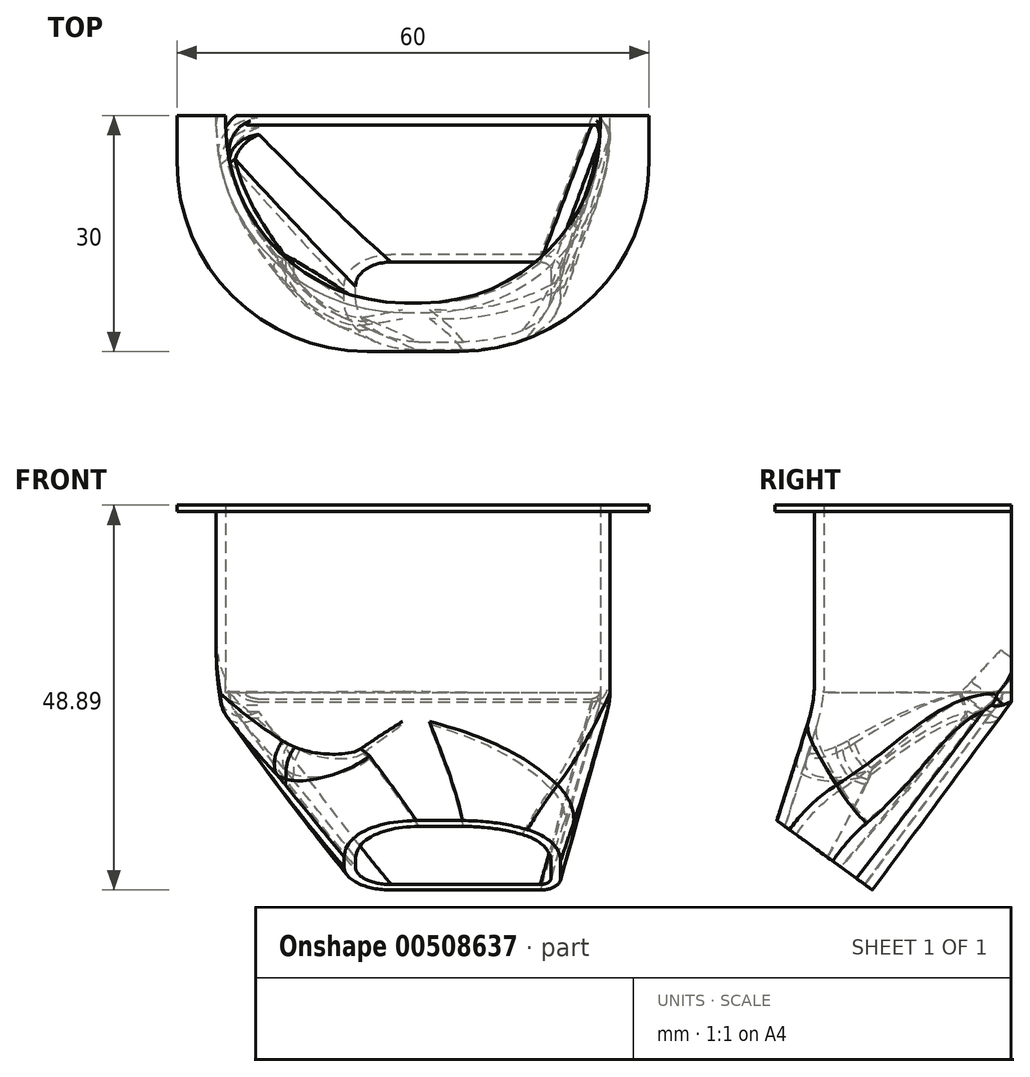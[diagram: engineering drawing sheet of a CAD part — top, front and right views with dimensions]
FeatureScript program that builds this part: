
annotation { "Feature Type Name" : "Feature", "Feature Type Description" : "" }
export const myFeature = defineFeature(function(context is Context, id is Id, definition is map)
    precondition{}
    {
        {
            var Q0;
            Q0=qCreatedBy(makeId("Front.planeOp"),FACE);
            var sketch = newSketch(context, id + "F0", { "sketchPlane" : qUnion([Q0])});
            skLineSegment(sketch, "E0.bottom", {"start": v(-25, 25) * mm, "end": v(25, 25) * mm});
            skLineSegment(sketch, "E0.top", {"start": v(-25, 0) * mm, "end": v(25, 0) * mm});
            skLineSegment(sketch, "E0.left", {"start": v(-25, 25) * mm, "end": v(-25, 0) * mm});
            skLineSegment(sketch, "E0.right", {"start": v(25, 25) * mm, "end": v(25, 0) * mm});
            skSolve(sketch);
        }
        {
            var Q0;
            Q0=makeQuery(id+"F0.imprint","IMPRINT",FACE,{"disambiguationData":[TD([[makeQuery(id+"F0.imprint","IMPRINT",EDGE,{"derivedFrom":sQuery(id+"F0.wireOp",EDGE,"E0.bottom")}),-1.0]])]});
            extrude(context, id + "F1", {"entities" : qUnion([Q0]), "endBound" : BoundingType.SYMMETRIC, "depth" : 25 * mm});
        }
        {
            var Q0;
            Q0=makeQuery(id+"F1.opExtrude","SWEPT_FACE",FACE,{"disambiguationData":[OSD([sQuery(id+"F0.wireOp",EDGE,"E0.bottom")])]});
            var Q1;
            Q1=makeQuery(id+"F1.opExtrude","CAP_FACE",FACE,{"disambiguationData":[OSD([sQuery(id+"F0.wireOp",EDGE,"E0.bottom"),sQuery(id+"F0.wireOp",EDGE,"E0.top"),sQuery(id+"F0.wireOp",EDGE,"E0.left"),sQuery(id+"F0.wireOp",EDGE,"E0.right")])],"isStart":true});
            shell(context, id + "F2", {"entities" : qUnion([Q0, Q1]), "thickness" : 1.2 * mm});
        }
        {
            var Q0;
            Q0=makeQuery(id+"F1.opExtrude","SWEPT_FACE",FACE,{"disambiguationData":[OSD([sQuery(id+"F0.wireOp",EDGE,"E0.right")])]});
            var sketch = newSketch(context, id + "F3", { "sketchPlane" : qUnion([Q0])});
            skLineSegment(sketch, "E1.bottom", {"start": v(-12.5, 25) * mm, "end": v(12.5, 25) * mm});
            skLineSegment(sketch, "E1.top", {"start": v(-12.5, 24.2) * mm, "end": v(12.5, 24.2) * mm});
            skLineSegment(sketch, "E1.left", {"start": v(-12.5, 25) * mm, "end": v(-12.5, 24.2) * mm});
            skLineSegment(sketch, "E1.right", {"start": v(12.5, 25) * mm, "end": v(12.5, 24.2) * mm});
            skSolve(sketch);
        }
        {
            var Q0;
            Q0=makeQuery(id+"F3.imprint","IMPRINT",FACE,{"disambiguationData":[TD([[makeQuery(id+"F3.imprint","IMPRINT",EDGE,{"derivedFrom":sQuery(id+"F3.wireOp",EDGE,"E1.bottom")}),-1.0]])]});
            extrude(context, id + "F4", {"entities" : qUnion([Q0]), "operationType" : NewBodyOperationType.ADD, "depth" : 5 * mm});
        }
        {
            var Q0;
            Q0=makeQuery(id+"F1.opExtrude","SWEPT_FACE",FACE,{"disambiguationData":[OSD([sQuery(id+"F0.wireOp",EDGE,"E0.left")])]});
            var sketch = newSketch(context, id + "F5", { "sketchPlane" : qUnion([Q0])});
            skLineSegment(sketch, "E2.bottom", {"start": v(-12.5, 25) * mm, "end": v(12.5, 25) * mm});
            skLineSegment(sketch, "E2.top", {"start": v(-12.5, 24.2) * mm, "end": v(12.5, 24.2) * mm});
            skLineSegment(sketch, "E2.left", {"start": v(-12.5, 25) * mm, "end": v(-12.5, 24.2) * mm});
            skLineSegment(sketch, "E2.right", {"start": v(12.5, 25) * mm, "end": v(12.5, 24.2) * mm});
            skSolve(sketch);
        }
        {
            var Q0;
            Q0=makeQuery(id+"F5.imprint","IMPRINT",FACE,{"disambiguationData":[TD([[makeQuery(id+"F5.imprint","IMPRINT",EDGE,{"derivedFrom":sQuery(id+"F5.wireOp",EDGE,"E2.bottom")}),1.0]])]});
            extrude(context, id + "F6", {"entities" : qUnion([Q0]), "operationType" : NewBodyOperationType.ADD, "depth" : 5 * mm});
        }
        {
            var Q0;
            Q0=makeQuery(id+"F6.boolean.opBoolean","MERGE",FACE,{"derivedFrom":[makeQuery(id+"F4.boolean.opBoolean","MERGE",FACE,{"derivedFrom":[makeQuery(id+"F1.opExtrude","CAP_FACE",FACE,{"disambiguationData":[OSD([sQuery(id+"F0.wireOp",EDGE,"E0.bottom"),sQuery(id+"F0.wireOp",EDGE,"E0.top"),sQuery(id+"F0.wireOp",EDGE,"E0.left"),sQuery(id+"F0.wireOp",EDGE,"E0.right")])],"isStart":false}),makeQuery(id+"F4.opExtrude","SWEPT_FACE",FACE,{"disambiguationData":[OSD([sQuery(id+"F3.wireOp",EDGE,"E1.left")])]})]}),makeQuery(id+"F6.opExtrude","SWEPT_FACE",FACE,{"disambiguationData":[OSD([sQuery(id+"F5.wireOp",EDGE,"E2.right")])]})]});
            var sketch = newSketch(context, id + "F7", { "sketchPlane" : qUnion([Q0])});
            skLineSegment(sketch, "E3.bottom", {"start": v(-30, 25) * mm, "end": v(30, 25) * mm});
            skLineSegment(sketch, "E3.top", {"start": v(-30, 24.2) * mm, "end": v(30, 24.2) * mm});
            skLineSegment(sketch, "E3.left", {"start": v(-30, 25) * mm, "end": v(-30, 24.2) * mm});
            skLineSegment(sketch, "E3.right", {"start": v(30, 25) * mm, "end": v(30, 24.2) * mm});
            skSolve(sketch);
        }
        {
            var Q0;
            Q0=makeQuery(id+"F7.imprint","IMPRINT",FACE,{"disambiguationData":[TD([[makeQuery(id+"F7.imprint","IMPRINT",EDGE,{"derivedFrom":sQuery(id+"F7.wireOp",EDGE,"E3.bottom")}),-1.0]])]});
            extrude(context, id + "F8", {"entities" : qUnion([Q0]), "operationType" : NewBodyOperationType.ADD, "depth" : 5 * mm});
        }
        {
            var Q0;
            Q0=qCreatedBy(makeId("Right.planeOp"),FACE);
            var sketch = newSketch(context, id + "F9", { "sketchPlane" : qUnion([Q0])});
            skPoint(sketch, "E4", {"position": v(15, -20) * mm});
            skSolve(sketch);
        }
        {
            var Q0;
            Q0=makeQuery(id+"F1.opExtrude","CAP_VERTEX",VERTEX,{"disambiguationData":[OSD([sQuery(id+"F0.wireOp",EDGE,"E0.top"),sQuery(id+"F0.wireOp",EDGE,"E0.left")])],"isStart":false});
            var Q1;
            Q1=makeQuery(id+"F1.opExtrude","CAP_VERTEX",VERTEX,{"disambiguationData":[OSD([sQuery(id+"F0.wireOp",EDGE,"E0.top"),sQuery(id+"F0.wireOp",EDGE,"E0.right")])],"isStart":false});
            var Q2;
            Q2=sQuery(id+"F9.wireOp",VERTEX,"E4");
            cPlane(context, id + "F10", {"entities" : qUnion([Q0, Q1, Q2]), "cplaneType" : CPlaneType.THREE_POINT, "offset" : 25.4 * mm, "width" : 152.4 * mm, "height" : 152.4 * mm});
        }
        {
            var Q0;
            Q0=qCreatedBy(id+"F10.planeOp",FACE);
            cPlane(context, id + "F11", {"entities" : qUnion([Q0]), "cplaneType" : CPlaneType.OFFSET, "offset" : 15 * mm, "width" : 152.4 * mm, "height" : 152.4 * mm});
        }
        {
            var Q0;
            Q0=qCreatedBy(id+"F11.planeOp",FACE);
            var sketch = newSketch(context, id + "F12", { "sketchPlane" : qUnion([Q0])});
            skEllipse(sketch, "E5", {"center": v(5, -2.4) * mm, "majorRadius": 13.75 * mm, "minorRadius": 7.5 * mm, "majorAxis": v(1, 0)});
            skSolve(sketch);
        }
        {
            var Q0;
            Q0=qCreatedBy(id+"F11.planeOp",FACE);
            var sketch = newSketch(context, id + "F13", { "sketchPlane" : qUnion([Q0])});
            skLineSegment(sketch, "E6.bottom", {"start": v(18.75, 5.1) * mm, "end": v(-8.75, 5.1) * mm});
            skLineSegment(sketch, "E6.top", {"start": v(18.75, -9.9) * mm, "end": v(-8.75, -9.9) * mm});
            skLineSegment(sketch, "E6.left", {"start": v(18.75, 5.1) * mm, "end": v(18.75, -9.9) * mm});
            skLineSegment(sketch, "E6.right", {"start": v(-8.75, 5.1) * mm, "end": v(-8.75, -9.9) * mm});
            skSolve(sketch);
        }
        {
            var Q1;
            Q1=makeQuery(id+"F1.opExtrude","SWEPT_FACE",FACE,{"disambiguationData":[OSD([sQuery(id+"F0.wireOp",EDGE,"E0.top")])]});
            var Q2;
            Q2=makeQuery(id+"F13.imprint","IMPRINT",FACE,{"disambiguationData":[TD([[makeQuery(id+"F13.imprint","IMPRINT",EDGE,{"derivedFrom":sQuery(id+"F13.wireOp",EDGE,"E6.bottom")}),1.0]])]});
            loft(context, id + "F14", {"operationType" : NewBodyOperationType.ADD, "sheetProfilesArray" : [{ "sheetProfileEntities" : qUnion([Q1]) }, { "sheetProfileEntities" : qUnion([Q2]) }]});
        }
        {
            var Q0;
            {var subQ0=sQuery(id+"F0.wireOp",EDGE,"E0.right");Q0=makeQuery(id+"F2.opShell","OFFSET_EDGE",EDGE,{"disambiguationData":[OSD([subQ0]),TDD([makeQuery(id+"F1.opExtrude","CAP_EDGE",EDGE,{"disambiguationData":[OSD([subQ0])],"isStart":false})])]});}
            var Q1;
            {var subQ0=sQuery(id+"F0.wireOp",EDGE,"E0.left");Q1=makeQuery(id+"F2.opShell","OFFSET_EDGE",EDGE,{"disambiguationData":[OSD([subQ0]),TDD([makeQuery(id+"F1.opExtrude","CAP_EDGE",EDGE,{"disambiguationData":[OSD([subQ0])],"isStart":false})])]});}
            fillet(context, id + "F15", {"entities" : qUnion([Q0, Q1]), "radius" : 22.7 * mm, "tangentPropagation" : true, "allowEdgeOverflow" : false});
        }
        {
            var Q0;
            {var subQ0=sQuery(id+"F0.wireOp",EDGE,"E0.top");var subQ1=makeQuery(id+"F1.opExtrude","CAP_EDGE",EDGE,{"disambiguationData":[OSD([subQ0])],"isStart":false});var subQ2=sQuery(id+"F0.wireOp",EDGE,"E0.right");var subQ3=sQuery(id+"F0.wireOp",EDGE,"E0.left");Q0=makeQuery(id+"F14.boolean.opBoolean","MERGE",EDGE,{"derivedFrom":[subQ1,makeQuery(id+"F14.opLoft","MID_CAP_EDGE",EDGE,{"disambiguationData":[OSD([subQ0,subQ3,subQ2]),TDD([makeQuery(id+"F1.opExtrude","CAP_VERTEX",VERTEX,{"disambiguationData":[OSD([subQ0,subQ3])],"isStart":false}),makeQuery(id+"F1.opExtrude","CAP_VERTEX",VERTEX,{"disambiguationData":[OSD([subQ0,subQ2])],"isStart":false}),subQ1])],"capPos":0.0})]});}
            fillet(context, id + "F16", {"entities" : qUnion([Q0]), "radius" : 16.8 * mm, "tangentPropagation" : true, "allowEdgeOverflow" : false});
        }
        {
            var Q0;
            {var subQ0=sQuery(id+"F0.wireOp",EDGE,"E0.right");var subQ1=sQuery(id+"F0.wireOp",EDGE,"E0.top");var subQ2=makeQuery(id+"F1.opExtrude","CAP_EDGE",EDGE,{"disambiguationData":[OSD([subQ1])],"isStart":false});var subQ3=sQuery(id+"F0.wireOp",EDGE,"E0.left");Q0=makeQuery(id+"F16.opFillet","BLEND_EDGE",EDGE,{"blendedFrom":[makeQuery(id+"F14.boolean.opBoolean","MERGE",EDGE,{"derivedFrom":[subQ2,makeQuery(id+"F14.opLoft","MID_CAP_EDGE",EDGE,{"disambiguationData":[OSD([subQ1,subQ3,subQ0]),TDD([makeQuery(id+"F1.opExtrude","CAP_VERTEX",VERTEX,{"disambiguationData":[OSD([subQ1,subQ3])],"isStart":false}),makeQuery(id+"F1.opExtrude","CAP_VERTEX",VERTEX,{"disambiguationData":[OSD([subQ1,subQ0])],"isStart":false}),subQ2])],"capPos":0.0})]}),makeQuery(id+"F1.opExtrude","SWEPT_FACE",FACE,{"disambiguationData":[OSD([subQ0])]})],"blendedInto":[makeQuery(id+"F1.opExtrude","SWEPT_FACE",FACE,{"disambiguationData":[OSD([subQ0])]})]});}
            fillet(context, id + "F17", {"entities" : qUnion([Q0]), "radius" : 22.94 * mm, "tangentPropagation" : true, "allowEdgeOverflow" : false});
        }
        {
            var Q0;
            Q0=makeQuery(id+"F14.opLoft","SWEPT_EDGE",EDGE,{"disambiguationData":[OSD([sQuery(id+"F0.wireOp",EDGE,"E0.top"),sQuery(id+"F0.wireOp",EDGE,"E0.right"),sQuery(id+"F13.wireOp",EDGE,"E6.top"),sQuery(id+"F13.wireOp",EDGE,"E6.left")])]});
            fillet(context, id + "F18", {"entities" : qUnion([Q0]), "radius" : 2.53 * mm, "tangentPropagation" : true, "allowEdgeOverflow" : false});
        }
        {
            var Q0;
            {var subQ0=sQuery(id+"F0.wireOp",EDGE,"E0.right");var subQ1=sQuery(id+"F0.wireOp",EDGE,"E0.top");var subQ2=makeQuery(id+"F1.opExtrude","CAP_EDGE",EDGE,{"disambiguationData":[OSD([subQ1])],"isStart":false});var subQ3=sQuery(id+"F0.wireOp",EDGE,"E0.left");Q0=makeQuery(id+"F17.opFillet","BLEND_EDGE",EDGE,{"blendedFrom":[makeQuery(id+"F16.opFillet","BLEND_EDGE",EDGE,{"blendedFrom":[makeQuery(id+"F14.boolean.opBoolean","MERGE",EDGE,{"derivedFrom":[subQ2,makeQuery(id+"F14.opLoft","MID_CAP_EDGE",EDGE,{"disambiguationData":[OSD([subQ1,subQ3,subQ0]),TDD([makeQuery(id+"F1.opExtrude","CAP_VERTEX",VERTEX,{"disambiguationData":[OSD([subQ1,subQ3])],"isStart":false}),makeQuery(id+"F1.opExtrude","CAP_VERTEX",VERTEX,{"disambiguationData":[OSD([subQ1,subQ0])],"isStart":false}),subQ2])],"capPos":0.0})]}),makeQuery(id+"F1.opExtrude","SWEPT_FACE",FACE,{"disambiguationData":[OSD([subQ0])]})],"blendedInto":[makeQuery(id+"F1.opExtrude","SWEPT_FACE",FACE,{"disambiguationData":[OSD([subQ0])]})]}),makeQuery(id+"F14.opLoft","SWEPT_FACE",FACE,{"disambiguationData":[OSD([subQ1,subQ0,sQuery(id+"F13.wireOp",EDGE,"E6.bottom"),sQuery(id+"F13.wireOp",EDGE,"E6.top"),sQuery(id+"F13.wireOp",EDGE,"E6.left")])]})],"blendedInto":[makeQuery(id+"F14.opLoft","SWEPT_FACE",FACE,{"disambiguationData":[OSD([subQ1,subQ0,sQuery(id+"F13.wireOp",EDGE,"E6.bottom"),sQuery(id+"F13.wireOp",EDGE,"E6.top"),sQuery(id+"F13.wireOp",EDGE,"E6.left")])]})]});}
            fillet(context, id + "F19", {"entities" : qUnion([Q0]), "radius" : 2 * mm, "tangentPropagation" : true, "allowEdgeOverflow" : false});
        }
        {
            var Q0;
            Q0=makeQuery(id+"F14.opLoft","SWEPT_EDGE",EDGE,{"disambiguationData":[OSD([sQuery(id+"F0.wireOp",EDGE,"E0.top"),sQuery(id+"F0.wireOp",EDGE,"E0.left"),sQuery(id+"F13.wireOp",EDGE,"E6.bottom"),sQuery(id+"F13.wireOp",EDGE,"E6.right")])]});
            fillet(context, id + "F20", {"entities" : qUnion([Q0]), "radius" : 9.17 * mm, "tangentPropagation" : true, "allowEdgeOverflow" : false});
        }
        {
            var Q0;
            Q0=makeQuery(id+"F14.opLoft","SWEPT_EDGE",EDGE,{"disambiguationData":[OSD([sQuery(id+"F0.wireOp",EDGE,"E0.top"),sQuery(id+"F0.wireOp",EDGE,"E0.left"),sQuery(id+"F13.wireOp",EDGE,"E6.top"),sQuery(id+"F13.wireOp",EDGE,"E6.right")])]});
            fillet(context, id + "F21", {"entities" : qUnion([Q0]), "radius" : 5 * mm, "tangentPropagation" : true, "allowEdgeOverflow" : false});
        }
        {
            var Q0;
            {var subQ0=sQuery(id+"F0.wireOp",EDGE,"E0.right");var subQ1=sQuery(id+"F0.wireOp",EDGE,"E0.left");var subQ2=sQuery(id+"F0.wireOp",EDGE,"E0.top");var subQ3=makeQuery(id+"F1.opExtrude","CAP_EDGE",EDGE,{"disambiguationData":[OSD([subQ2])],"isStart":false});Q0=makeQuery(id+"F17.opFillet","BLEND_EDGE",EDGE,{"blendedFrom":[makeQuery(id+"F16.opFillet","BLEND_EDGE",EDGE,{"blendedFrom":[makeQuery(id+"F14.boolean.opBoolean","MERGE",EDGE,{"derivedFrom":[subQ3,makeQuery(id+"F14.opLoft","MID_CAP_EDGE",EDGE,{"disambiguationData":[OSD([subQ2,subQ1,subQ0]),TDD([makeQuery(id+"F1.opExtrude","CAP_VERTEX",VERTEX,{"disambiguationData":[OSD([subQ2,subQ1])],"isStart":false}),makeQuery(id+"F1.opExtrude","CAP_VERTEX",VERTEX,{"disambiguationData":[OSD([subQ2,subQ0])],"isStart":false}),subQ3])],"capPos":0.0})]}),makeQuery(id+"F1.opExtrude","SWEPT_FACE",FACE,{"disambiguationData":[OSD([subQ0])]})],"blendedInto":[makeQuery(id+"F1.opExtrude","SWEPT_FACE",FACE,{"disambiguationData":[OSD([subQ0])]})]}),makeQuery(id+"F14.opLoft","SWEPT_FACE",FACE,{"disambiguationData":[OSD([subQ2,subQ1,subQ0,sQuery(id+"F13.wireOp",EDGE,"E6.bottom"),sQuery(id+"F13.wireOp",EDGE,"E6.left"),sQuery(id+"F13.wireOp",EDGE,"E6.right")])]})],"blendedInto":[makeQuery(id+"F14.opLoft","SWEPT_FACE",FACE,{"disambiguationData":[OSD([subQ2,subQ1,subQ0,sQuery(id+"F13.wireOp",EDGE,"E6.bottom"),sQuery(id+"F13.wireOp",EDGE,"E6.left"),sQuery(id+"F13.wireOp",EDGE,"E6.right")])]})]});}
            fillet(context, id + "F22", {"entities" : qUnion([Q0]), "radius" : 18 * mm, "tangentPropagation" : true, "allowEdgeOverflow" : false});
        }
        {
            var Q0;
            {var subQ0=sQuery(id+"F13.wireOp",EDGE,"E6.left");var subQ1=sQuery(id+"F13.wireOp",EDGE,"E6.bottom");var subQ2=sQuery(id+"F0.wireOp",EDGE,"E0.right");var subQ3=sQuery(id+"F0.wireOp",EDGE,"E0.top");var subQ4=sQuery(id+"F0.wireOp",EDGE,"E0.left");var subQ5=makeQuery(id+"F1.opExtrude","CAP_EDGE",EDGE,{"disambiguationData":[OSD([subQ3])],"isStart":false});Q0=makeQuery(id+"F22.opFillet","BLEND_EDGE",EDGE,{"blendedFrom":[makeQuery(id+"F17.opFillet","BLEND_EDGE",EDGE,{"blendedFrom":[makeQuery(id+"F16.opFillet","BLEND_EDGE",EDGE,{"blendedFrom":[makeQuery(id+"F14.boolean.opBoolean","MERGE",EDGE,{"derivedFrom":[subQ5,makeQuery(id+"F14.opLoft","MID_CAP_EDGE",EDGE,{"disambiguationData":[OSD([subQ3,subQ4,subQ2]),TDD([makeQuery(id+"F1.opExtrude","CAP_VERTEX",VERTEX,{"disambiguationData":[OSD([subQ3,subQ4])],"isStart":false}),makeQuery(id+"F1.opExtrude","CAP_VERTEX",VERTEX,{"disambiguationData":[OSD([subQ3,subQ2])],"isStart":false}),subQ5])],"capPos":0.0})]}),makeQuery(id+"F1.opExtrude","SWEPT_FACE",FACE,{"disambiguationData":[OSD([subQ2])]})],"blendedInto":[makeQuery(id+"F1.opExtrude","SWEPT_FACE",FACE,{"disambiguationData":[OSD([subQ2])]})]}),makeQuery(id+"F14.opLoft","SWEPT_FACE",FACE,{"disambiguationData":[OSD([subQ3,subQ4,subQ2,subQ1,subQ0,sQuery(id+"F13.wireOp",EDGE,"E6.right")])]})],"blendedInto":[makeQuery(id+"F14.opLoft","SWEPT_FACE",FACE,{"disambiguationData":[OSD([subQ3,subQ4,subQ2,subQ1,subQ0,sQuery(id+"F13.wireOp",EDGE,"E6.right")])]})]}),makeQuery(id+"F14.opLoft","SWEPT_FACE",FACE,{"disambiguationData":[OSD([subQ3,subQ2,subQ1,sQuery(id+"F13.wireOp",EDGE,"E6.top"),subQ0])]})],"blendedInto":[makeQuery(id+"F14.opLoft","SWEPT_FACE",FACE,{"disambiguationData":[OSD([subQ3,subQ2,subQ1,sQuery(id+"F13.wireOp",EDGE,"E6.top"),subQ0])]})]});}
            fillet(context, id + "F23", {"entities" : qUnion([Q0]), "radius" : 7.8 * mm, "tangentPropagation" : true, "allowEdgeOverflow" : false});
        }
        {
            var Q0;
            Q0=makeQuery(id+"F1.opExtrude","CAP_EDGE",EDGE,{"disambiguationData":[OSD([sQuery(id+"F0.wireOp",EDGE,"E0.left")])],"isStart":false});
            fillet(context, id + "F24", {"entities" : qUnion([Q0]), "radius" : 23.66 * mm, "tangentPropagation" : true, "allowEdgeOverflow" : false});
        }
        {
            var Q0;
            {var subQ0=sQuery(id+"F0.wireOp",EDGE,"E0.left");Q0=makeQuery(id+"F24.opFillet","BLEND_EDGE",EDGE,{"blendedFrom":[makeQuery(id+"F1.opExtrude","CAP_EDGE",EDGE,{"disambiguationData":[OSD([subQ0])],"isStart":false}),makeQuery(id+"F20.opFillet","BLEND_FACE",FACE,{"disambiguationData":[OSD([sQuery(id+"F0.wireOp",EDGE,"E0.top"),subQ0,sQuery(id+"F0.wireOp",EDGE,"E0.right"),sQuery(id+"F13.wireOp",EDGE,"E6.bottom"),sQuery(id+"F13.wireOp",EDGE,"E6.top"),sQuery(id+"F13.wireOp",EDGE,"E6.right")])]})],"blendedInto":[makeQuery(id+"F20.opFillet","BLEND_FACE",FACE,{"disambiguationData":[OSD([sQuery(id+"F0.wireOp",EDGE,"E0.top"),subQ0,sQuery(id+"F0.wireOp",EDGE,"E0.right"),sQuery(id+"F13.wireOp",EDGE,"E6.bottom"),sQuery(id+"F13.wireOp",EDGE,"E6.top"),sQuery(id+"F13.wireOp",EDGE,"E6.right")])]})]});}
            fillet(context, id + "F25", {"entities" : qUnion([Q0]), "radius" : 5 * mm, "tangentPropagation" : true, "allowEdgeOverflow" : false});
        }
        {
            var Q0;
            Q0=makeQuery(id+"F2.opShell","OFFSET_FACE",FACE,{"disambiguationData":[OSD([sQuery(id+"F0.wireOp",EDGE,"E0.top")])]});
            var Q1;
            Q1=makeQuery(id+"F14.opLoft","CAP_FACE",FACE,{"disambiguationData":[OSD([makeQuery(id+"F13.imprint","IMPRINT",FACE,{"disambiguationData":[TD([[makeQuery(id+"F13.imprint","IMPRINT",EDGE,{"derivedFrom":sQuery(id+"F13.wireOp",EDGE,"E6.bottom")}),1.0]])]})])],"isStart":true});
            shell(context, id + "F26", {"entities" : qUnion([Q0, Q1]), "thickness" : 1.2 * mm});
        }
        {
            var Q0;
            {var subQ0=sQuery(id+"F0.wireOp",EDGE,"E0.right");Q0=makeQuery(id+"F15.opFillet","BLEND_EDGE",EDGE,{"blendedFrom":[makeQuery(id+"F2.opShell","OFFSET_EDGE",EDGE,{"disambiguationData":[OSD([subQ0]),TDD([makeQuery(id+"F1.opExtrude","CAP_EDGE",EDGE,{"disambiguationData":[OSD([subQ0])],"isStart":false})])]}),makeQuery(id+"F2.opShell","OFFSET_FACE",FACE,{"disambiguationData":[OSD([sQuery(id+"F0.wireOp",EDGE,"E0.top")])]})],"blendedInto":[makeQuery(id+"F2.opShell","OFFSET_FACE",FACE,{"disambiguationData":[OSD([sQuery(id+"F0.wireOp",EDGE,"E0.top")])]})]});}
            var Q1;
            {var subQ0=sQuery(id+"F0.wireOp",EDGE,"E0.top");Q1=makeQuery(id+"F2.opShell","OFFSET_EDGE",EDGE,{"disambiguationData":[OSD([subQ0]),TDD([makeQuery(id+"F1.opExtrude","CAP_EDGE",EDGE,{"disambiguationData":[OSD([subQ0])],"isStart":false})])]});}
            fillet(context, id + "F27", {"entities" : qUnion([Q0, Q1]), "radius" : .25 * mm, "tangentPropagation" : true, "allowEdgeOverflow" : false});
        }
        {
            var Q0;
            Q0=makeQuery(id+"F26.opShell","OFFSET_EDGE",EDGE,{"disambiguationData":[OSD([sQuery(id+"F0.wireOp",EDGE,"E0.top")])]});
            var Q1;
            {var subQ0=sQuery(id+"F0.wireOp",EDGE,"E0.top");Q1=makeQuery(id+"F26.opShell","TWEAK_EDGE",EDGE,{"disambiguationData":[OD(0.0)],"derivedFrom":[makeQuery(id+"F2.opShell","OFFSET_FACE",FACE,{"disambiguationData":[OSD([subQ0])]}),makeQuery(id+"F19.opFillet","BLEND_FACE",FACE,{"disambiguationData":[OSD([subQ0,sQuery(id+"F0.wireOp",EDGE,"E0.right"),sQuery(id+"F13.wireOp",EDGE,"E6.top"),sQuery(id+"F13.wireOp",EDGE,"E6.left")])]})]});}
            var Q2;
            {var subQ0=sQuery(id+"F0.wireOp",EDGE,"E0.top");Q2=makeQuery(id+"F26.opShell","TWEAK_EDGE",EDGE,{"derivedFrom":[makeQuery(id+"F2.opShell","OFFSET_FACE",FACE,{"disambiguationData":[OSD([subQ0])]}),makeQuery(id+"F21.opFillet","BLEND_FACE",FACE,{"disambiguationData":[OSD([subQ0,sQuery(id+"F0.wireOp",EDGE,"E0.left"),sQuery(id+"F13.wireOp",EDGE,"E6.top"),sQuery(id+"F13.wireOp",EDGE,"E6.right")])]})]});}
            fillet(context, id + "F28", {"entities" : qUnion([Q0, Q1, Q2]), "radius" : .5 * mm, "tangentPropagation" : true, "allowEdgeOverflow" : false});
        }
        {
            var Q0;
            Q0=makeQuery(id+"F8.opExtrude","CAP_EDGE",EDGE,{"disambiguationData":[OSD([sQuery(id+"F7.wireOp",EDGE,"E3.left")])],"isStart":false});
            var Q1;
            Q1=makeQuery(id+"F8.opExtrude","CAP_EDGE",EDGE,{"disambiguationData":[OSD([sQuery(id+"F7.wireOp",EDGE,"E3.right")])],"isStart":false});
            fillet(context, id + "F29", {"entities" : qUnion([Q0, Q1]), "radius" : 24.14 * mm, "tangentPropagation" : true, "allowEdgeOverflow" : false});
        }
    });
